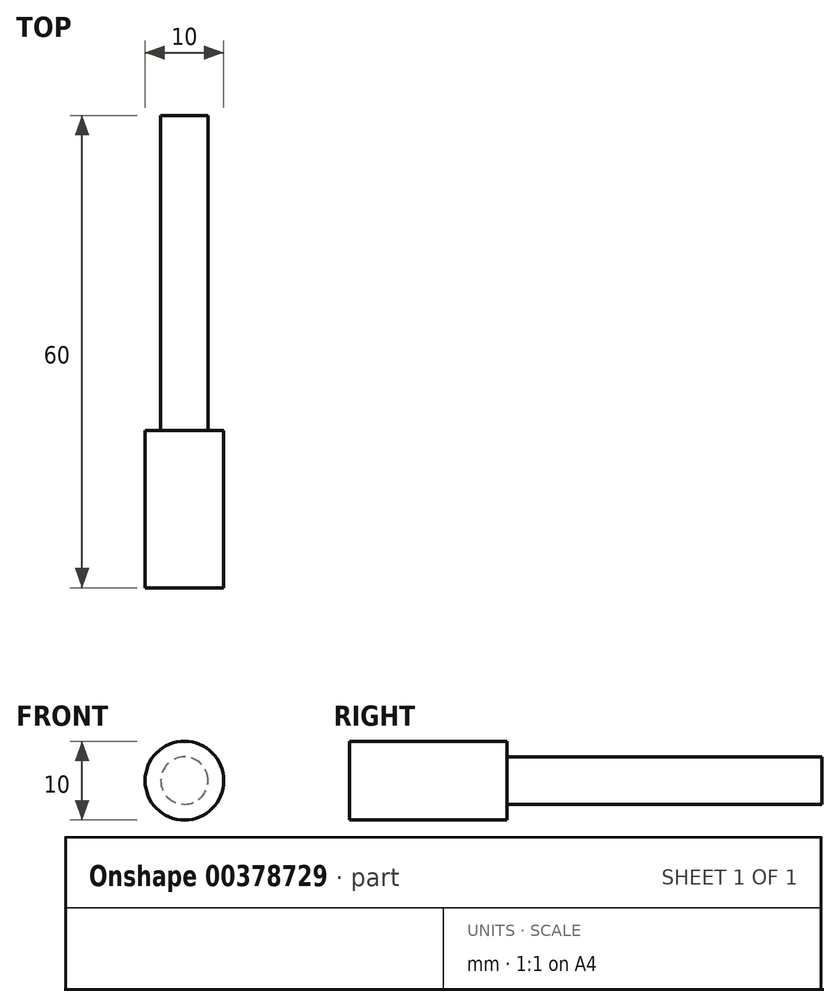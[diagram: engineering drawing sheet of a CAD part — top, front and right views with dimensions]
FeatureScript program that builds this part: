
annotation { "Feature Type Name" : "Feature", "Feature Type Description" : "" }
export const myFeature = defineFeature(function(context is Context, id is Id, definition is map)
    precondition{}
    {
        {
            var Q0;
            Q0=qCreatedBy(makeId("Right.planeOp"),FACE);
            var sketch = newSketch(context, id + "F0", { "sketchPlane" : qUnion([Q0])});
            skLineSegment(sketch, "E0", {"start": v(0, 0) * mm, "end": v(0, 5) * mm});
            skLineSegment(sketch, "E1", {"start": v(0, 5) * mm, "end": v(20, 5) * mm});
            skLineSegment(sketch, "E2", {"start": v(20, 5) * mm, "end": v(20, 3) * mm});
            skLineSegment(sketch, "E3", {"start": v(20, 3) * mm, "end": v(60, 3) * mm});
            skLineSegment(sketch, "E4", {"start": v(60, 3) * mm, "end": v(60, 0) * mm});
            skLineSegment(sketch, "E5", {"start": v(60, 0) * mm, "end": v(0, 0) * mm});
            skLineSegment(sketch, "E6.MirrorCS", {"start": v(0, 0) * mm, "end": v(0, -5) * mm, "construction": true});
            skLineSegment(sketch, "E7.MirrorCS", {"start": v(0, -5) * mm, "end": v(20, -5) * mm, "construction": true});
            skLineSegment(sketch, "E8.MirrorCS", {"start": v(20, -5) * mm, "end": v(20, -3) * mm, "construction": true});
            skLineSegment(sketch, "E9.MirrorCS", {"start": v(20, -3) * mm, "end": v(60, -3) * mm, "construction": true});
            skLineSegment(sketch, "E10.MirrorCS", {"start": v(60, -3) * mm, "end": v(60, 0) * mm, "construction": true});
            skSolve(sketch);
        }
        {
            var Q0;
            Q0 = qSketchRegion(id + "F0", true);
            var Q1;
            Q1=sQuery(id+"F0.wireOp",EDGE,"E5");
            revolve(context, id + "F1", {"entities" : qUnion([Q0]), "axis" : qUnion([Q1]), "revolveType" : RevolveType.FULL});
        }
    });
